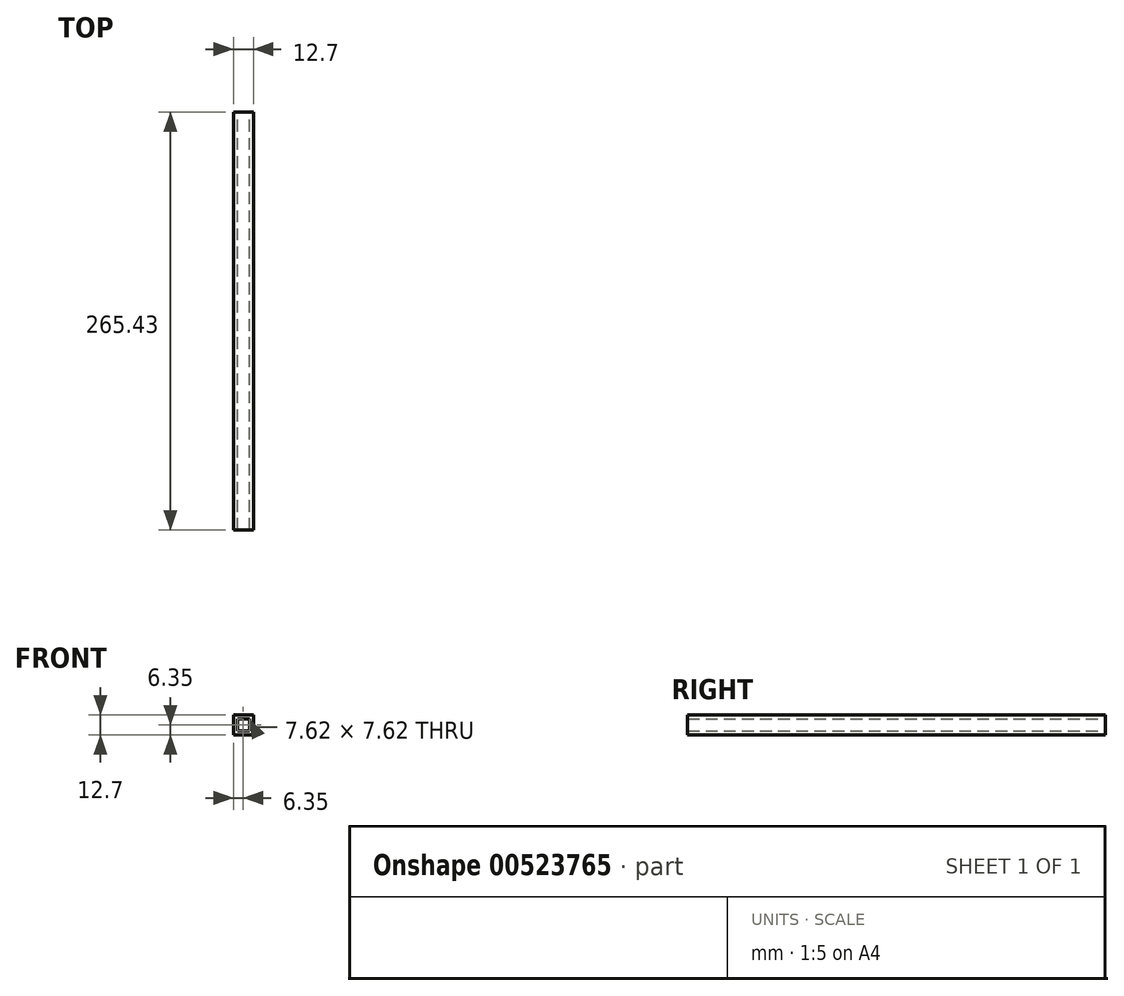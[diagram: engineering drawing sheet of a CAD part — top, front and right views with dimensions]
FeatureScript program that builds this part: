
annotation { "Feature Type Name" : "Feature", "Feature Type Description" : "" }
export const myFeature = defineFeature(function(context is Context, id is Id, definition is map)
    precondition{}
    {
        {
            var Q0;
            Q0=qCreatedBy(makeId("Front.planeOp"),FACE);
            var sketch = newSketch(context, id + "F0", { "sketchPlane" : qUnion([Q0])});
            skLineSegment(sketch, "E0.bottom", {"start": v(0, 0) * mm, "end": v(-12.7, 0) * mm});
            skLineSegment(sketch, "E0.top", {"start": v(0, 12.7) * mm, "end": v(-12.7, 12.7) * mm});
            skLineSegment(sketch, "E0.left", {"start": v(0, 0) * mm, "end": v(0, 12.7) * mm});
            skLineSegment(sketch, "E0.right", {"start": v(-12.7, 0) * mm, "end": v(-12.7, 12.7) * mm});
            skLineSegment(sketch, "E1", {"start": v(-12.7, 12.7) * mm, "end": v(-10.16, 12.7) * mm});
            skLineSegment(sketch, "E2", {"start": v(-10.16, 12.7) * mm, "end": v(-10.16, 10.16) * mm});
            skLineSegment(sketch, "E3.bottom", {"start": v(-10.16, 10.16) * mm, "end": v(-2.54, 10.16) * mm});
            skLineSegment(sketch, "E3.top", {"start": v(-10.16, 2.54) * mm, "end": v(-2.54, 2.54) * mm});
            skLineSegment(sketch, "E3.left", {"start": v(-10.16, 10.16) * mm, "end": v(-10.16, 2.54) * mm});
            skLineSegment(sketch, "E3.right", {"start": v(-2.54, 10.16) * mm, "end": v(-2.54, 2.54) * mm});
            skSolve(sketch);
        }
        {
            var Q0;
            Q0=makeQuery(id+"F0.imprint","IMPRINT",FACE,{"disambiguationData":[TD([[makeQuery(id+"F0.imprint","IMPRINT",EDGE,{"derivedFrom":sQuery(id+"F0.wireOp",EDGE,"E0.bottom")}),-1.0]])]});
            extrude(context, id + "F1", {"entities" : qUnion([Q0]), "depth" : 265.43 * mm, "offsetDistance" : 25.4 * mm});
        }
    });
